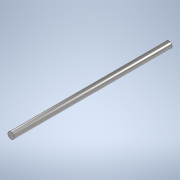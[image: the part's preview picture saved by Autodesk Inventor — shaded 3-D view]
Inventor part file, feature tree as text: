
AUTODESK INVENTOR PART (.ipt)
format: ipt  version: 2020 (Build 240168000, 168)  size: 92,672 bytes
history: native  units: mm
features: extrude x1, sketch x1
ambient origin geometry x8: Origin, YZ Plane, XZ Plane, XY Plane, X Axis, Y Axis, Z Axis, Center Point
bodies: Solid1 (feature_tree)
feature tree (2):
  extrude  "Extrusion1"  Depth=290.0mm TaperAngle=0.0deg
  sketch  "Sketch1"  dims[d0=12.0mm d1=290.0mm d2=0.0mm]
